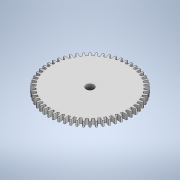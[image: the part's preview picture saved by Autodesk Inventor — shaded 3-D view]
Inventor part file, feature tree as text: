
AUTODESK INVENTOR PART (.ipt)
format: ipt  version: 2020 (Build 240168000, 168)  size: 393,216 bytes
history: native  units: in
note: dims shown in document units (in); Inventor stores cm internally (conversion verified against a paired STEP export)
features: extrude x2, sketch x2
ambient origin geometry x8: Origin, YZ Plane, XZ Plane, XY Plane, X Axis, Y Axis, Z Axis, Center Point
bodies: Body1 (feature_tree)
feature tree (4):
  extrude  "Extrusion2"  Depth=2.3622in
  extrude  "Extrusion3"  Depth=0.1575in TaperAngle=0.0deg
  sketch  "Sketch1"  dims[d0=2.5984in d4=2.3622in]
  sketch  "Sketch3"  dims[d9=22.0472in d11=360.0deg d13=0.1575in d14=0.0in d15=0.2362in d16=0.1575in d17=0.0in]
